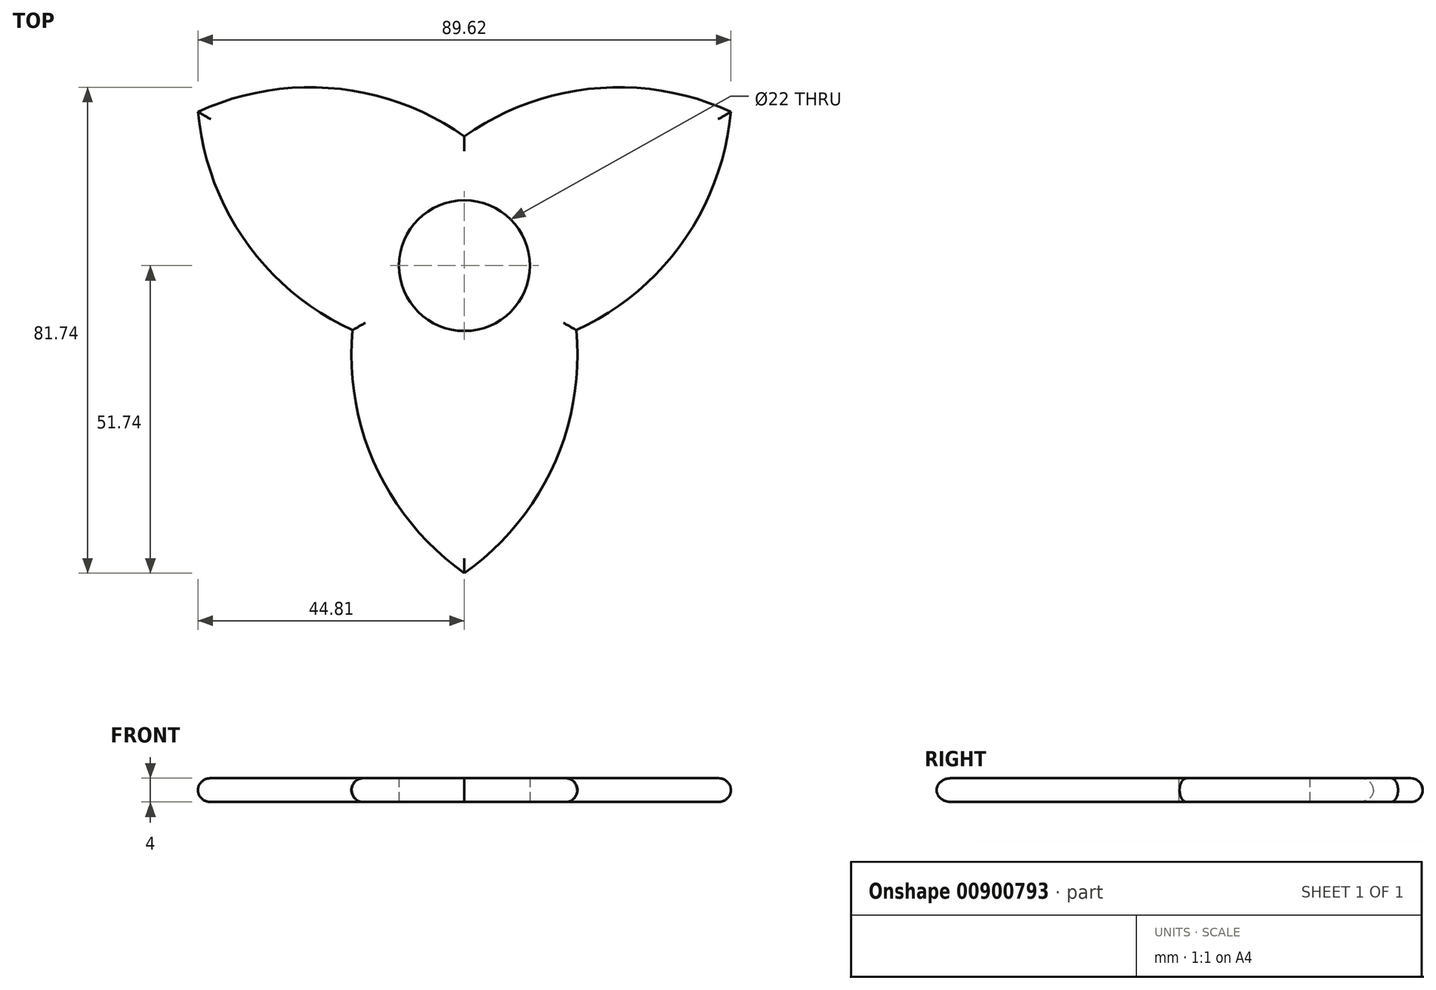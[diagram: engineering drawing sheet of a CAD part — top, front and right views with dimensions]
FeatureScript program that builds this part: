
annotation { "Feature Type Name" : "Feature", "Feature Type Description" : "" }
export const myFeature = defineFeature(function(context is Context, id is Id, definition is map)
    precondition{}
    {
        {
            var Q0;
            Q0=qCreatedBy(makeId("Top.planeOp"),FACE);
            var sketch = newSketch(context, id + "F0", { "sketchPlane" : qUnion([Q0])});
            skArc(sketch, "E0", {"start": v(-44.81, 25.87) * mm, "mid": v(-36.74, 4.02) * mm, "end": v(-18.83, -10.87) * mm});
            skArc(sketch, "E1.1.0", {"start": v(0, -51.74) * mm, "mid": v(14.9, -33.83) * mm, "end": v(18.83, -10.87) * mm});
            skArc(sketch, "E1.2.0", {"start": v(44.81, 25.87) * mm, "mid": v(21.85, 29.81) * mm, "end": v(0, 21.74) * mm});
            skPoint(sketch, "E1.center", {"position": v(0, 0) * mm});
            skArc(sketch, "E2.trimOffspring", {"start": v(18.83, -10.87) * mm, "mid": v(36.74, 4.02) * mm, "end": v(44.81, 25.87) * mm});
            skArc(sketch, "E3.trimOffspring", {"start": v(-18.83, -10.87) * mm, "mid": v(-14.9, -33.83) * mm, "end": v(0, -51.74) * mm});
            skArc(sketch, "E4.trimOffspring", {"start": v(0, 21.74) * mm, "mid": v(-21.85, 29.81) * mm, "end": v(-44.81, 25.87) * mm});
            skCircle(sketch, "E5", {"center": v(0, 0) * mm, "radius": 11 * mm});
            skSolve(sketch);
        }
        {
            var Q0;
            Q0=makeQuery(id+"F0.imprint","IMPRINT",FACE,{"disambiguationData":[TD([[makeQuery(id+"F0.imprint","IMPRINT",EDGE,{"derivedFrom":sQuery(id+"F0.wireOp",EDGE,"E0")}),1.0]])]});
            extrude(context, id + "F1", {"entities" : qUnion([Q0]), "endBound" : BoundingType.SYMMETRIC, "depth" : 4 * mm, "offsetDistance" : 25 * mm});
        }
        {
            var Q0;
            Q0=makeQuery(id+"F1.opExtrude","CAP_EDGE",EDGE,{"disambiguationData":[OSD([sQuery(id+"F0.wireOp",EDGE,"E2.trimOffspring")])],"isStart":true});
            var Q1;
            Q1=makeQuery(id+"F1.opExtrude","CAP_EDGE",EDGE,{"disambiguationData":[OSD([sQuery(id+"F0.wireOp",EDGE,"E2.trimOffspring")])],"isStart":false});
            var Q2;
            Q2=makeQuery(id+"F1.opExtrude","CAP_EDGE",EDGE,{"disambiguationData":[OSD([sQuery(id+"F0.wireOp",EDGE,"E0")])],"isStart":true});
            var Q3;
            Q3=makeQuery(id+"F1.opExtrude","CAP_EDGE",EDGE,{"disambiguationData":[OSD([sQuery(id+"F0.wireOp",EDGE,"E1.2.0")])],"isStart":true});
            var Q4;
            Q4=makeQuery(id+"F1.opExtrude","CAP_EDGE",EDGE,{"disambiguationData":[OSD([sQuery(id+"F0.wireOp",EDGE,"E1.1.0")])],"isStart":false});
            var Q5;
            Q5=makeQuery(id+"F1.opExtrude","CAP_EDGE",EDGE,{"disambiguationData":[OSD([sQuery(id+"F0.wireOp",EDGE,"E1.1.0")])],"isStart":true});
            var Q6;
            Q6=makeQuery(id+"F1.opExtrude","CAP_EDGE",EDGE,{"disambiguationData":[OSD([sQuery(id+"F0.wireOp",EDGE,"E4.trimOffspring")])],"isStart":true});
            var Q7;
            Q7=makeQuery(id+"F1.opExtrude","CAP_EDGE",EDGE,{"disambiguationData":[OSD([sQuery(id+"F0.wireOp",EDGE,"E4.trimOffspring")])],"isStart":false});
            var Q8;
            Q8=makeQuery(id+"F1.opExtrude","CAP_EDGE",EDGE,{"disambiguationData":[OSD([sQuery(id+"F0.wireOp",EDGE,"E0")])],"isStart":false});
            var Q9;
            Q9=makeQuery(id+"F1.opExtrude","CAP_EDGE",EDGE,{"disambiguationData":[OSD([sQuery(id+"F0.wireOp",EDGE,"E3.trimOffspring")])],"isStart":true});
            var Q10;
            Q10=makeQuery(id+"F1.opExtrude","CAP_EDGE",EDGE,{"disambiguationData":[OSD([sQuery(id+"F0.wireOp",EDGE,"E1.2.0")])],"isStart":false});
            var Q11;
            Q11=makeQuery(id+"F1.opExtrude","CAP_EDGE",EDGE,{"disambiguationData":[OSD([sQuery(id+"F0.wireOp",EDGE,"E3.trimOffspring")])],"isStart":false});
            fillet(context, id + "F2", {"entities" : qUnion([Q0, Q1, Q2, Q3, Q4, Q5, Q6, Q7, Q8, Q9, Q10, Q11]), "radius" : 2 * mm, "tangentPropagation" : true, "allowEdgeOverflow" : false});
        }
    });
